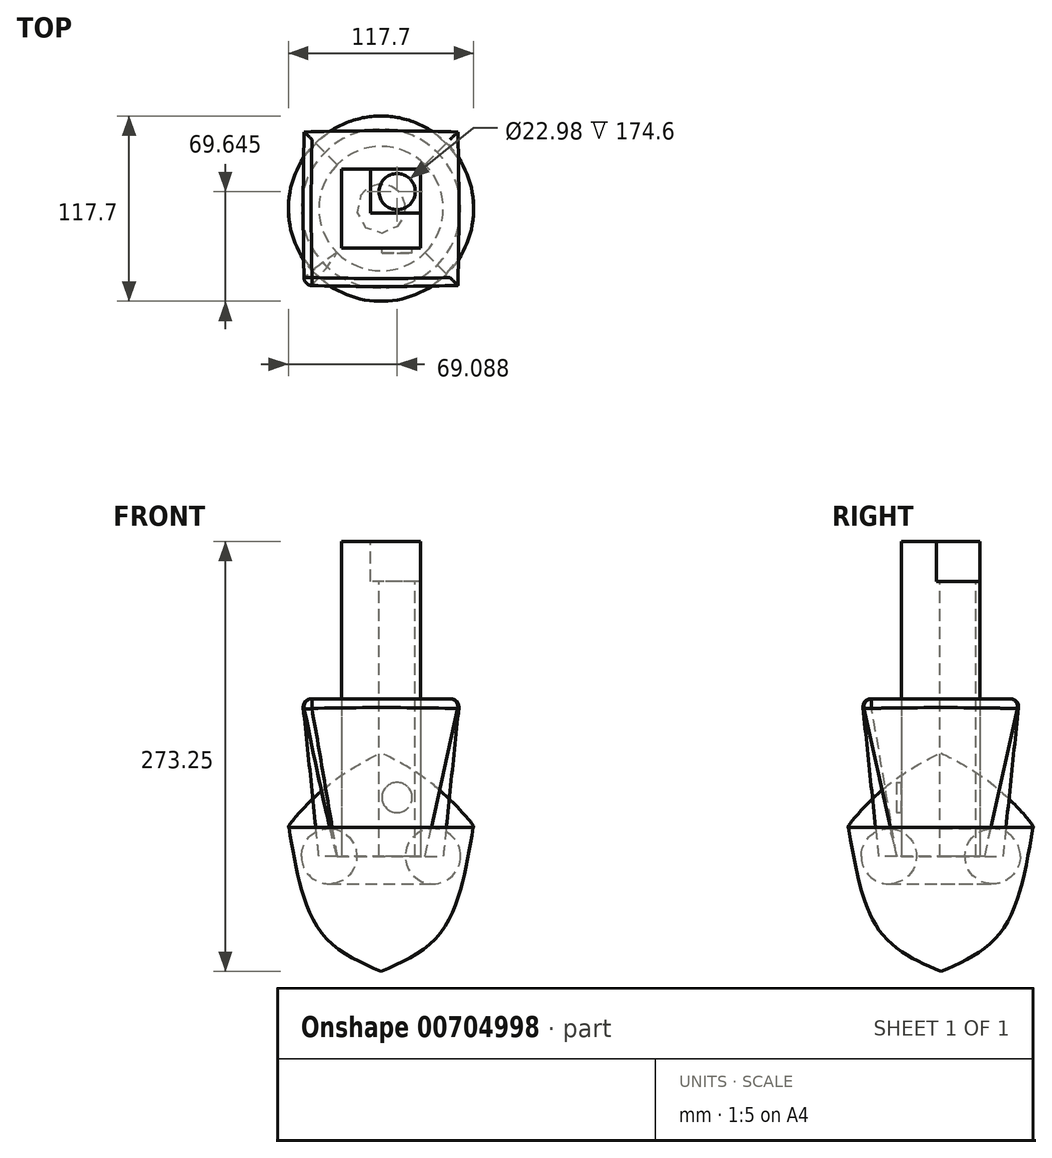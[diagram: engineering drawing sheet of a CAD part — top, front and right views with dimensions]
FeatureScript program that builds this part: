
annotation { "Feature Type Name" : "Feature", "Feature Type Description" : "" }
export const myFeature = defineFeature(function(context is Context, id is Id, definition is map)
    precondition{}
    {
        {
            var Q0;
            Q0=qCreatedBy(makeId("Top.planeOp"),FACE);
            var sketch = newSketch(context, id + "F0", { "sketchPlane" : qUnion([Q0])});
            skPoint(sketch, "E0.middle", {"position": v(0, 0) * mm});
            skLineSegment(sketch, "E1.bottom", {"start": v(25, -25) * mm, "end": v(-25, -25) * mm});
            skLineSegment(sketch, "E1.top", {"start": v(25, 25) * mm, "end": v(-25, 25) * mm});
            skLineSegment(sketch, "E1.left", {"start": v(25, -25) * mm, "end": v(25, 25) * mm});
            skLineSegment(sketch, "E1.right", {"start": v(-25, -25) * mm, "end": v(-25, 25) * mm});
            skSolve(sketch);
        }
        {
            var Q0;
            Q0=makeQuery(id+"F0.imprint","IMPRINT",FACE,{"disambiguationData":[TD([[makeQuery(id+"F0.imprint","IMPRINT",EDGE,{"derivedFrom":sQuery(id+"F0.wireOp",EDGE,"E1.bottom")}),-1.0]])]});
            extrude(context, id + "F1", {"entities" : qUnion([Q0]), "depth" : 200 * mm, "offsetDistance" : 25.4 * mm});
        }
        {
            var Q0;
            Q0=makeQuery(id+"F1.opExtrude","CAP_FACE",FACE,{"disambiguationData":[OSD([sQuery(id+"F0.wireOp",EDGE,"E1.bottom"),sQuery(id+"F0.wireOp",EDGE,"E1.top"),sQuery(id+"F0.wireOp",EDGE,"E1.left"),sQuery(id+"F0.wireOp",EDGE,"E1.right")])],"isStart":false});
            var sketch = newSketch(context, id + "F2", { "sketchPlane" : qUnion([Q0])});
            skLineSegment(sketch, "E2.bottom", {"start": v(-6.66, -2.78) * mm, "end": v(56.66, -2.78) * mm});
            skLineSegment(sketch, "E2.top", {"start": v(-6.66, 52.78) * mm, "end": v(56.66, 52.78) * mm});
            skLineSegment(sketch, "E2.left", {"start": v(-6.66, -2.78) * mm, "end": v(-6.66, 52.78) * mm});
            skLineSegment(sketch, "E2.right", {"start": v(56.66, -2.78) * mm, "end": v(56.66, 52.78) * mm});
            skPoint(sketch, "E2.middle", {"position": v(25, 25) * mm});
            skSolve(sketch);
        }
        {
            var Q0;
            Q0 = qSketchRegion(id + "F2", true);
            extrude(context, id + "F3", {"entities" : qUnion([Q0]), "operationType" : NewBodyOperationType.REMOVE, "oppositeDirection" : true, "depth" : 25.4 * mm, "offsetDistance" : 25.4 * mm});
        }
        {
            var Q0;
            Q0=makeQuery(id+"F3.boolean.opBoolean","COPY",FACE,{"derivedFrom":makeQuery(id+"F3.opExtrude","SWEPT_FACE",FACE,{"disambiguationData":[OSD([sQuery(id+"F2.wireOp",EDGE,"E2.bottom")])]})});
            var sketch = newSketch(context, id + "F4", { "sketchPlane" : qUnion([Q0])});
            skCircle(sketch, "E3", {"center": v(-10.16, 37.3) * mm, "radius": 9.61 * mm});
            skSolve(sketch);
        }
        {
            var Q0;
            Q0=makeQuery(id+"F4.imprint","IMPRINT",FACE,{"disambiguationData":[TD([[makeQuery(id+"F4.imprint","IMPRINT",EDGE,{"derivedFrom":sQuery(id+"F4.wireOp",EDGE,"E3")}),1.0]])]});
            extrude(context, id + "F5", {"entities" : qUnion([Q0]), "operationType" : NewBodyOperationType.ADD, "oppositeDirection" : true, "depth" : 25.4 * mm, "offsetDistance" : 25.4 * mm});
        }
        {
            var Q0;
            Q0=makeQuery(id+"F3.boolean.opBoolean","COPY",FACE,{"derivedFrom":makeQuery(id+"F3.opExtrude","CAP_FACE",FACE,{"disambiguationData":[OSD([sQuery(id+"F2.wireOp",EDGE,"E2.bottom"),sQuery(id+"F2.wireOp",EDGE,"E2.top"),sQuery(id+"F2.wireOp",EDGE,"E2.left"),sQuery(id+"F2.wireOp",EDGE,"E2.right")])],"isStart":false})});
            var sketch = newSketch(context, id + "F6", { "sketchPlane" : qUnion([Q0])});
            skCircle(sketch, "E4", {"center": v(10.24, 10.8) * mm, "radius": 11.49 * mm});
            skSolve(sketch);
        }
        {
            var Q0;
            Q0=makeQuery(id+"F6.imprint","IMPRINT",FACE,{"disambiguationData":[TD([[makeQuery(id+"F6.imprint","IMPRINT",EDGE,{"derivedFrom":sQuery(id+"F6.wireOp",EDGE,"E4")}),1.0]])]});
            extrude(context, id + "F7", {"entities" : qUnion([Q0]), "operationType" : NewBodyOperationType.REMOVE, "endBound" : BoundingType.UP_TO_NEXT, "oppositeDirection" : true, "depth" : 25.4 * mm, "offsetDistance" : 25.4 * mm});
        }
        {
            var Q0;
            Q0=qCreatedBy(makeId("Right.planeOp"),FACE);
            var sketch = newSketch(context, id + "F8", { "sketchPlane" : qUnion([Q0])});
            skLineSegment(sketch, "E5", {"start": v(0, 65.76) * mm, "end": v(0, -73.25) * mm});
            skFitSpline(sketch, "E6", {"points": [v(0, 65.76) * mm, v(36.4, 42.74) * mm, v(58.86, 18.56) * mm, v(58.57, 18.28) * mm], "startDerivative": vector(70.56, -36.19) * mm, "endDerivative": vector(-8.72, -3) * mm});
            skFitSpline(sketch, "E7", {"points": [v(58.57, 18.28) * mm, v(38.42, -47.92) * mm, v(0, -73.25) * mm], "startDerivative": vector(-23.1, -137.75) * mm, "endDerivative": vector(-96.53, -42.05) * mm});
            skSolve(sketch);
        }
        {
            var Q0;
            Q0=makeQuery(id+"F8.imprint","IMPRINT",FACE,{"disambiguationData":[TD([[makeQuery(id+"F8.imprint","IMPRINT",EDGE,{"derivedFrom":sQuery(id+"F8.wireOp",EDGE,"E5")}),1.0]])]});
            var Q1;
            Q1=sQuery(id+"F8.wireOp",EDGE,"E5");
            var Q2;
            Q2=sQuery(id+"F8.wireOp",EDGE,"E5");
            revolve(context, id + "F9", {"surfaceOperationType" : NewSurfaceOperationType.ADD, "entities" : qUnion([Q0]), "surfaceEntities" : qUnion([Q1]), "axis" : qUnion([Q2]), "revolveType" : RevolveType.FULL});
        }
        {
            var Q0;
            Q0=qCreatedBy(makeId("Front.planeOp"),FACE);
            var sketch = newSketch(context, id + "F10", { "sketchPlane" : qUnion([Q0])});
            skCircle(sketch, "E8", {"center": v(-32.95, 0) * mm, "radius": 17.56 * mm});
            skCircle(sketch, "E9.cCircle", {"center": v(-32.95, 0) * mm, "radius": 17.56 * mm, "construction": true});
            skLineSegment(sketch, "E9.0", {"start": v(-13.92, -4.16) * mm, "end": v(-24.34, -17.48) * mm});
            skLineSegment(sketch, "E9.1", {"start": v(-24.34, -17.48) * mm, "end": v(-41.25, -17.63) * mm});
            skLineSegment(sketch, "E9.2", {"start": v(-41.25, -17.63) * mm, "end": v(-51.91, -4.5) * mm});
            skLineSegment(sketch, "E9.3", {"start": v(-51.91, -4.5) * mm, "end": v(-48.3, 12.01) * mm});
            skLineSegment(sketch, "E9.4", {"start": v(-48.3, 12.01) * mm, "end": v(-33.13, 19.49) * mm});
            skLineSegment(sketch, "E9.5", {"start": v(-33.13, 19.49) * mm, "end": v(-17.83, 12.29) * mm});
            skLineSegment(sketch, "E9.6", {"start": v(-17.83, 12.29) * mm, "end": v(-13.92, -4.16) * mm});
            skPoint(sketch, "E9.0.midPoint", {"position": v(-19.13, -10.82) * mm});
            skSolve(sketch);
        }
        {
            var Q0;
            Q0=qCreatedBy(makeId("Right.planeOp"),FACE);
            var sketch = newSketch(context, id + "F11", { "sketchPlane" : qUnion([Q0])});
            skLineSegment(sketch, "E10", {"start": v(0, 0) * mm, "end": v(0, 43.68) * mm});
            skLineSegment(sketch, "E11", {"start": v(0, 0) * mm, "end": v(0, -38.03) * mm});
            skSolve(sketch);
        }
        {
            var Q0;
            Q0=makeQuery(id+"F10.imprint","IMPRINT",FACE,{"disambiguationData":[TD([[makeQuery(id+"F10.imprint","IMPRINT",EDGE,{"derivedFrom":sQuery(id+"F10.wireOp",EDGE,"E8")}),1.0]])]});
            var Q1;
            Q1=sQuery(id+"F11.wireOp",EDGE,"E11");
            revolve(context, id + "F12", {"surfaceOperationType" : NewSurfaceOperationType.NEW, "entities" : qUnion([Q0]), "axis" : qUnion([Q1]), "revolveType" : RevolveType.FULL});
        }
        {
            var Q0;
            Q0=qCreatedBy(makeId("Top.planeOp"),FACE);
            cPlane(context, id + "F13", {"entities" : qUnion([Q0]), "cplaneType" : CPlaneType.OFFSET, "offset" : 100 * mm, "width" : 152.4 * mm, "height" : 152.4 * mm});
        }
        {
            var Q0;
            Q0=qCreatedBy(id+"F13.planeOp",FACE);
            var sketch = newSketch(context, id + "F14", { "sketchPlane" : qUnion([Q0])});
            skLineSegment(sketch, "E12.bottom", {"start": v(50, -50) * mm, "end": v(-50, -50) * mm});
            skLineSegment(sketch, "E12.top", {"start": v(50, 50) * mm, "end": v(-50, 50) * mm});
            skLineSegment(sketch, "E12.left", {"start": v(50, -50) * mm, "end": v(50, 50) * mm});
            skLineSegment(sketch, "E12.right", {"start": v(-50, -50) * mm, "end": v(-50, 50) * mm});
            skPoint(sketch, "E12.middle", {"position": v(0, 0) * mm});
            skSolve(sketch);
        }
        {
            var Q0;
            Q0=qCreatedBy(makeId("Top.planeOp"),FACE);
            var sketch = newSketch(context, id + "F15", { "sketchPlane" : qUnion([Q0])});
            skCircle(sketch, "E13", {"center": v(0, 0) * mm, "radius": 39.5 * mm});
            skSolve(sketch);
        }
        {
            var Q0;
            Q0=makeQuery(id+"F15.imprint","IMPRINT",FACE,{"disambiguationData":[TD([[makeQuery(id+"F15.imprint","IMPRINT",EDGE,{"derivedFrom":sQuery(id+"F15.wireOp",EDGE,"E13")}),1.0]])]});
            var Q1;
            Q1=makeQuery(id+"F14.imprint","IMPRINT",FACE,{"disambiguationData":[TD([[makeQuery(id+"F14.imprint","IMPRINT",EDGE,{"derivedFrom":sQuery(id+"F14.wireOp",EDGE,"E12.bottom")}),-1.0]])]});
            loft(context, id + "F16", {"sheetProfilesArray" : [{ "sheetProfileEntities" : qUnion([Q0]) }, { "sheetProfileEntities" : qUnion([Q1]) }]});
        }
        {
            var Q0;
            Q0=makeQuery(id+"F16.opLoft","MID_CAP_EDGE",EDGE,{"disambiguationData":[OSD([sQuery(id+"F14.wireOp",EDGE,"E12.top"),sQuery(id+"F14.wireOp",EDGE,"E12.left"),sQuery(id+"F14.wireOp",EDGE,"E12.right")])],"capPos":1.0});
            var Q1;
            Q1=makeQuery(id+"F16.opLoft","CAP_FACE",FACE,{"disambiguationData":[OSD([makeQuery(id+"F14.imprint","IMPRINT",FACE,{"disambiguationData":[TD([[makeQuery(id+"F14.imprint","IMPRINT",EDGE,{"derivedFrom":sQuery(id+"F14.wireOp",EDGE,"E12.bottom")}),-1.0]])]})])],"isStart":true});
            var Q2;
            Q2=makeQuery(id+"F16.opLoft","MID_CAP_EDGE",EDGE,{"disambiguationData":[OSD([sQuery(id+"F14.wireOp",EDGE,"E12.bottom"),sQuery(id+"F14.wireOp",EDGE,"E12.top"),sQuery(id+"F14.wireOp",EDGE,"E12.right")])],"capPos":1.0});
            fillet(context, id + "F17", {"entities" : qUnion([Q0, Q1, Q2]), "radius" : 5.08 * mm, "tangentPropagation" : true, "allowEdgeOverflow" : false});
        }
        {
            var Q0;
            Q0=makeQuery(id+"F16.opLoft","SWEPT_EDGE",EDGE,{"disambiguationData":[OSD([sQuery(id+"F14.wireOp",EDGE,"E12.bottom"),sQuery(id+"F14.wireOp",EDGE,"E12.top"),sQuery(id+"F14.wireOp",EDGE,"E12.left"),sQuery(id+"F15.wireOp",EDGE,"E13")])]});
            fillet(context, id + "F18", {"entities" : qUnion([Q0]), "radius" : 5.08 * mm, "tangentPropagation" : true, "allowEdgeOverflow" : false});
        }
    });
